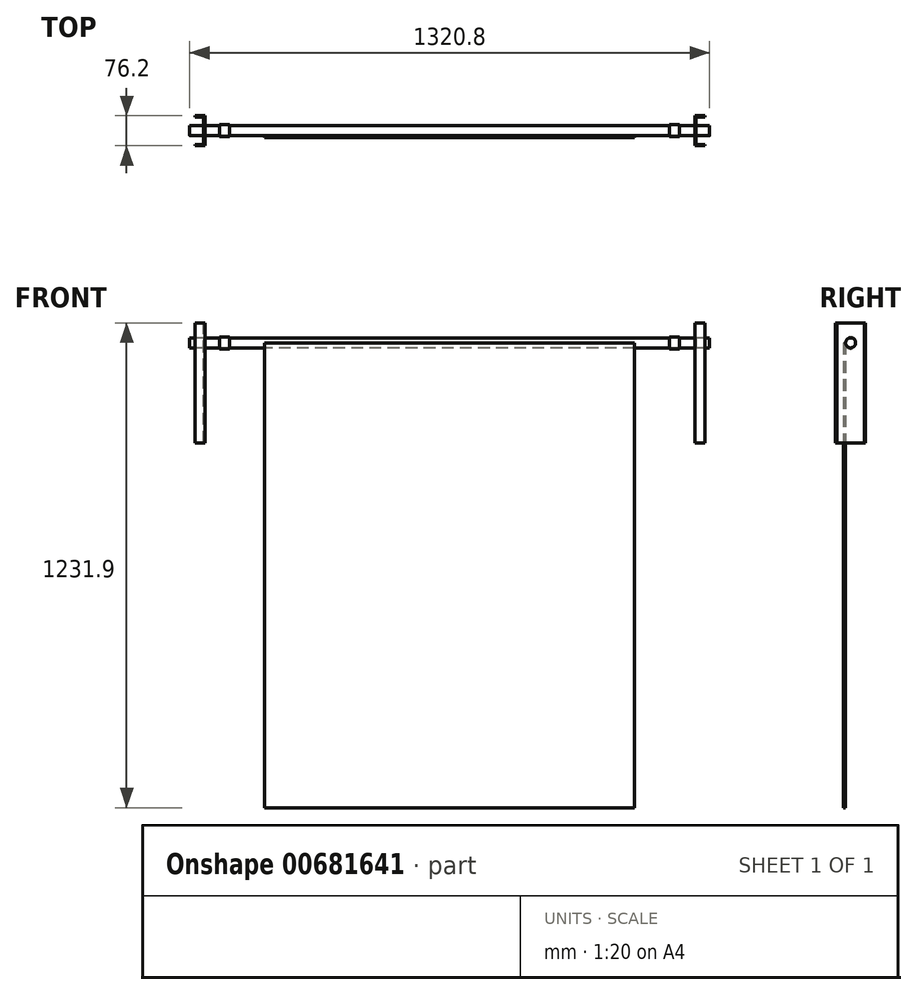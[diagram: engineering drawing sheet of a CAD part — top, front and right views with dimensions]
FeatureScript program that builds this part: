
annotation { "Feature Type Name" : "Feature", "Feature Type Description" : "" }
export const myFeature = defineFeature(function(context is Context, id is Id, definition is map)
    precondition{}
    {
        {
            var Q0;
            Q0=qCreatedBy(makeId("Right.planeOp"),FACE);
            var sketch = newSketch(context, id + "F0", { "sketchPlane" : qUnion([Q0])});
            skCircle(sketch, "E0", {"center": v(0, 0) * mm, "radius": 12.7 * mm});
            skArc(sketch, "E1", {"start": v(-1.58, -1181.09) * mm, "mid": v(-1007.78, -615.9) * mm, "end": v(-1051.78, 537.33) * mm, "construction": true});
            skLineSegment(sketch, "E2", {"start": v(-1061.72, -584.2) * mm, "end": v(-1061.72, 50.8) * mm});
            skLineSegment(sketch, "E3.bottom", {"start": v(-12.7, 0) * mm, "end": v(-17.77, 0) * mm});
            skLineSegment(sketch, "E3.top", {"start": v(-12.7, -1181.1) * mm, "end": v(-17.77, -1181.1) * mm});
            skLineSegment(sketch, "E3.left", {"start": v(-12.7, 0) * mm, "end": v(-12.7, -1181.1) * mm});
            skLineSegment(sketch, "E3.right", {"start": v(-17.77, 0) * mm, "end": v(-17.77, -1181.1) * mm});
            skLineSegment(sketch, "E4", {"start": v(0, 0) * mm, "end": v(0, 50.8) * mm, "construction": true});
            skLineSegment(sketch, "E5", {"start": v(0, 50.8) * mm, "end": v(55.88, 50.8) * mm});
            skLineSegment(sketch, "E6", {"start": v(55.88, 50.8) * mm, "end": v(-1061.72, 50.8) * mm});
            skSolve(sketch);
        }
        {
            var Q0;
            Q0=makeQuery(id+"F0.imprint","IMPRINT",FACE,{"disambiguationData":[TD([[makeQuery(id+"F0.imprint","IMPRINT",EDGE,{"derivedFrom":sQuery(id+"F0.wireOp",EDGE,"E0")}),1.0]])]});
            extrude(context, id + "F1", {"entities" : qUnion([Q0]), "endBound" : BoundingType.SYMMETRIC, "depth" : 1320.8 * mm, "offsetDistance" : 25.4 * mm});
        }
        {
            var Q0;
            Q0=makeQuery(id+"F0.imprint","IMPRINT",FACE,{"disambiguationData":[TD([[makeQuery(id+"F0.imprint","IMPRINT",EDGE,{"derivedFrom":sQuery(id+"F0.wireOp",EDGE,"E3.bottom")}),1.0]])]});
            extrude(context, id + "F2", {"entities" : qUnion([Q0]), "endBound" : BoundingType.SYMMETRIC, "depth" : 939.8 * mm, "offsetDistance" : 25.4 * mm});
        }
        {
            var Q0;
            Q0=sQuery(id+"F0.wireOp",EDGE,"E6");
            cPlane(context, id + "F3", {"entities" : qUnion([Q0]), "cplaneType" : CPlaneType.LINE_ANGLE, "offset" : 25.4 * mm, "angle" : 0 * degree, "width" : 152.4 * mm, "height" : 152.4 * mm});
        }
        {
            var Q0;
            Q0=qCreatedBy(id+"F3.planeOp",FACE);
            var sketch = newSketch(context, id + "F4", { "sketchPlane" : qUnion([Q0])});
            skLineSegment(sketch, "E7", {"start": v(-622.21, -0.02) * mm, "end": v(-622.21, -38.12) * mm});
            skLineSegment(sketch, "E8", {"start": v(-622.21, -38.12) * mm, "end": v(-647.61, -38.12) * mm});
            skLineSegment(sketch, "E9", {"start": v(-647.61, -38.12) * mm, "end": v(-647.61, -34.95) * mm});
            skLineSegment(sketch, "E10", {"start": v(-647.61, -34.95) * mm, "end": v(-625.39, -34.95) * mm});
            skLineSegment(sketch, "E11", {"start": v(-625.39, -34.95) * mm, "end": v(-625.39, 34.9) * mm});
            skLineSegment(sketch, "E12", {"start": v(-625.39, 34.9) * mm, "end": v(-647.61, 34.9) * mm});
            skLineSegment(sketch, "E13", {"start": v(-647.61, 34.9) * mm, "end": v(-647.61, 38.08) * mm});
            skLineSegment(sketch, "E14", {"start": v(-647.61, 38.08) * mm, "end": v(-622.21, 38.08) * mm});
            skLineSegment(sketch, "E15", {"start": v(-622.21, 38.08) * mm, "end": v(-622.21, -38.12) * mm});
            skLineSegment(sketch, "E16.MirrorCS", {"start": v(647.79, 34.9) * mm, "end": v(647.79, 38.08) * mm});
            skLineSegment(sketch, "E17.MirrorCS", {"start": v(647.79, -38.12) * mm, "end": v(647.79, -34.95) * mm});
            skLineSegment(sketch, "E18.MirrorCS", {"start": v(647.79, -34.95) * mm, "end": v(625.56, -34.95) * mm});
            skLineSegment(sketch, "E19.MirrorCS", {"start": v(625.56, -34.95) * mm, "end": v(625.56, 34.9) * mm});
            skLineSegment(sketch, "E20.MirrorCS", {"start": v(622.39, -38.12) * mm, "end": v(647.79, -38.12) * mm});
            skLineSegment(sketch, "E21.MirrorCS", {"start": v(647.79, 38.08) * mm, "end": v(622.39, 38.08) * mm});
            skLineSegment(sketch, "E22.MirrorCS", {"start": v(625.56, 34.9) * mm, "end": v(647.79, 34.9) * mm});
            skLineSegment(sketch, "E23.MirrorCS", {"start": v(622.39, 38.08) * mm, "end": v(622.39, -38.12) * mm});
            skLineSegment(sketch, "E24", {"start": v(0, 0) * mm, "end": v(558.8, 0) * mm, "construction": true});
            skLineSegment(sketch, "E25", {"start": v(558.8, 0) * mm, "end": v(558.8, 101.6) * mm, "construction": true});
            skSolve(sketch);
        }
        {
            var Q0;
            Q0 = qSketchRegion(id + "F4", true);
            extrude(context, id + "F5", {"entities" : qUnion([Q0]), "operationType" : NewBodyOperationType.ADD, "depth" : 304.8 * mm, "offsetDistance" : 25.4 * mm});
        }
        {
            var Q0;
            Q0=sQuery(id+"F4.wireOp",EDGE,"E25");
            cPlane(context, id + "F6", {"entities" : qUnion([Q0]), "cplaneType" : CPlaneType.LINE_ANGLE, "offset" : 25.4 * mm, "angle" : 90 * degree, "width" : 152.4 * mm, "height" : 152.4 * mm});
        }
        {
            var Q0;
            Q0=qCreatedBy(id+"F6.planeOp",FACE);
            var sketch = newSketch(context, id + "F7", { "sketchPlane" : qUnion([Q0])});
            skCircle(sketch, "E26", {"center": v(0, 0) * mm, "radius": 15.24 * mm});
            skSolve(sketch);
        }
        {
            var Q0;
            Q0=makeQuery(id+"F7.imprint","IMPRINT",FACE,{"disambiguationData":[TD([[makeQuery(id+"F7.imprint","IMPRINT",EDGE,{"derivedFrom":sQuery(id+"F7.wireOp",EDGE,"E26")}),1.0]])]});
            var Q1;
            Q1=sQuery(id+"F7.wireOp",EDGE,"E26");
            extrude(context, id + "F8", {"entities" : qUnion([Q0]), "surfaceEntities" : qUnion([Q1]), "depth" : 25.4 * mm, "offsetDistance" : 25.4 * mm});
        }
        {
            var Q0;
            Q0=makeQuery(id+"F8.opExtrude","SWEPT_BODY",BODY,{"disambiguationData":[OSD([sQuery(id+"F7.wireOp",EDGE,"E26")])]});
            var Q1;
            Q1=qCreatedBy(makeId("Right.planeOp"),FACE);
            mirror(context, id + "F9", {"entities" : qUnion([Q0]), "mirrorPlane" : qUnion([Q1])});
        }
    });
